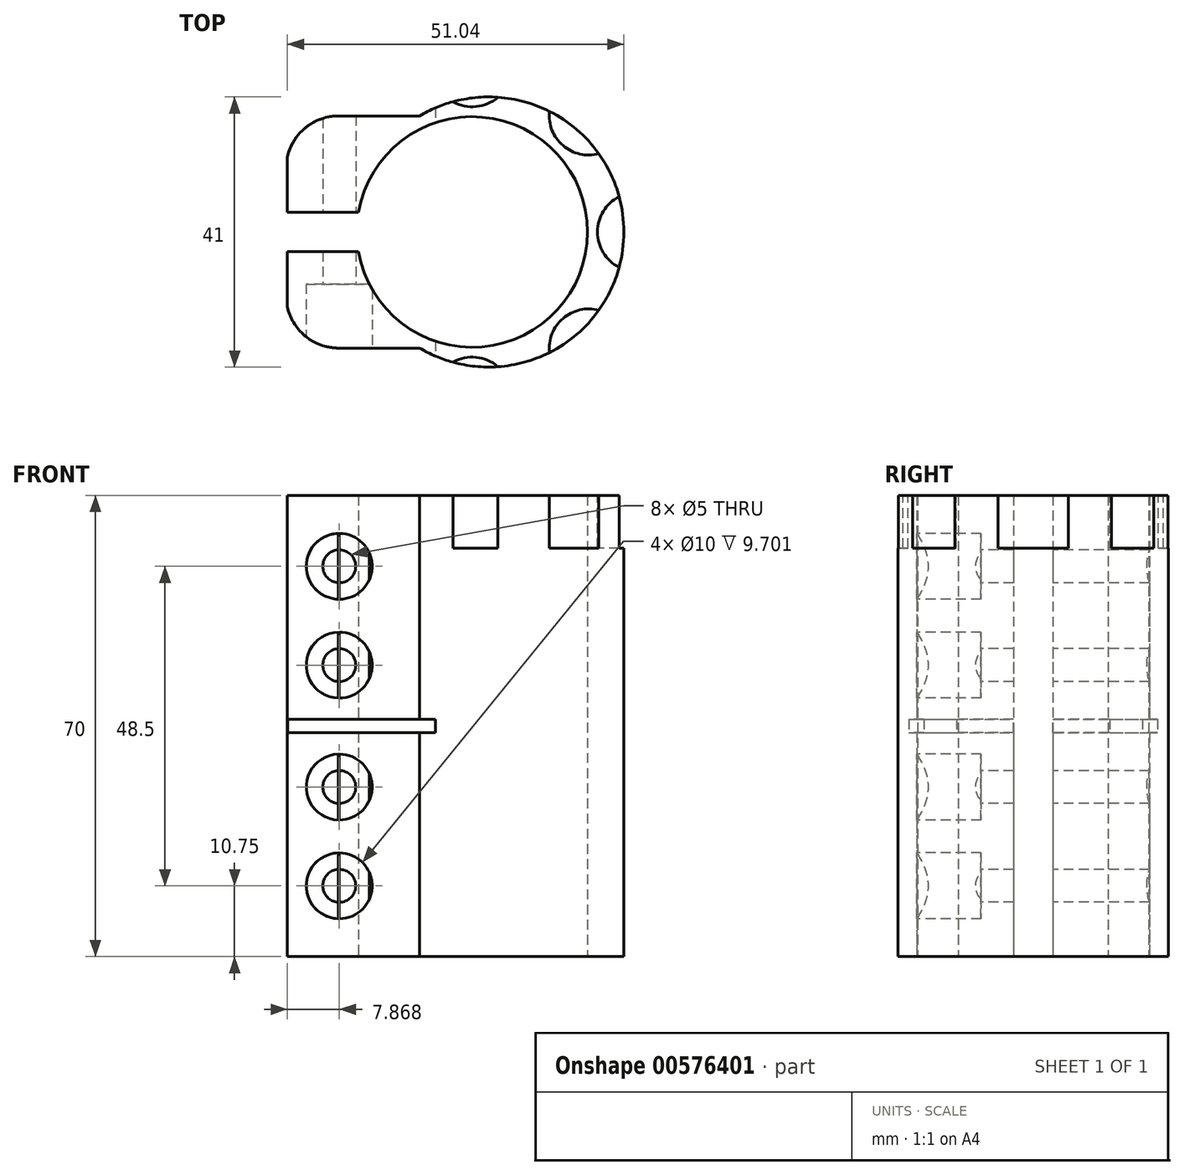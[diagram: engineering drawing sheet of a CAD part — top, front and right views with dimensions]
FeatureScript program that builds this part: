
annotation { "Feature Type Name" : "Feature", "Feature Type Description" : "" }
export const myFeature = defineFeature(function(context is Context, id is Id, definition is map)
    precondition{}
    {
        {
            var Q0;
            Q0=qCreatedBy(makeId("Top.planeOp"),FACE);
            var sketch = newSketch(context, id + "F0", { "sketchPlane" : qUnion([Q0])});
            skArc(sketch, "E0", {"start": v(-17.24, -2.98) * mm, "mid": v(17.5, 0) * mm, "end": v(-17.24, 2.98) * mm});
            skLineSegment(sketch, "E1", {"start": v(-7.97, 17.62) * mm, "end": v(-20.17, 17.62) * mm});
            skLineSegment(sketch, "E2", {"start": v(-28.04, 11.38) * mm, "end": v(-28.04, 2.98) * mm});
            skLineSegment(sketch, "E3", {"start": v(-28.04, 2.98) * mm, "end": v(-17.24, 2.98) * mm});
            skArc(sketch, "E4", {"start": v(-20.17, 17.62) * mm, "mid": v(-25.21, 15.9) * mm, "end": v(-28.04, 11.38) * mm});
            skLineSegment(sketch, "E5", {"start": v(0, 0) * mm, "end": v(37.47, 0) * mm});
            skLineSegment(sketch, "E6.MirrorCS", {"start": v(-28.04, -2.98) * mm, "end": v(-17.24, -2.98) * mm});
            skLineSegment(sketch, "E7.MirrorCS", {"start": v(-7.97, -17.62) * mm, "end": v(-20.17, -17.62) * mm});
            skLineSegment(sketch, "E8.MirrorCS", {"start": v(-28.04, -11.38) * mm, "end": v(-28.04, -2.98) * mm});
            skArc(sketch, "E9.MirrorCS", {"start": v(-20.17, -17.62) * mm, "mid": v(-25.21, -15.9) * mm, "end": v(-28.04, -11.38) * mm});
            skArc(sketch, "E10.trimOffspring", {"start": v(-7.97, -17.62) * mm, "mid": v(23, 0) * mm, "end": v(-7.97, 17.62) * mm});
            skSolve(sketch);
        }
        {
            var Q0;
            Q0 = qSketchRegion(id + "F0", true);
            extrude(context, id + "F1", {"entities" : qUnion([Q0]), "endBound" : BoundingType.SYMMETRIC, "depth" : 70 * mm, "offsetDistance" : 25 * mm});
        }
        {
            var Q0;
            Q0=makeQuery(id+"F1.opExtrude","SWEPT_FACE",FACE,{"disambiguationData":[OSD([sQuery(id+"F0.wireOp",EDGE,"E7.MirrorCS")])]});
            var sketch = newSketch(context, id + "F2", { "sketchPlane" : qUnion([Q0])});
            skPoint(sketch, "E11", {"position": v(-20.17, -9.25) * mm});
            skPoint(sketch, "E12", {"position": v(-20.17, -24.25) * mm});
            skPoint(sketch, "E13", {"position": v(-20.17, 9.25) * mm});
            skPoint(sketch, "E14", {"position": v(-20.17, 24.25) * mm});
            skSolve(sketch);
        }
        {
            var Q0;
            Q0=sQuery(id+"F2.wireOp",VERTEX,"E12");
            var Q1;
            Q1=sQuery(id+"F2.wireOp",VERTEX,"E11");
            var Q2;
            Q2=sQuery(id+"F2.wireOp",VERTEX,"E13");
            var Q3;
            Q3=sQuery(id+"F2.wireOp",VERTEX,"E14");
            var Q4;
            Q4=makeQuery(id+"F1.opExtrude","SWEPT_BODY",BODY,{"disambiguationData":[OSD([sQuery(id+"F0.wireOp",EDGE,"E0"),sQuery(id+"F0.wireOp",EDGE,"E1"),sQuery(id+"F0.wireOp",EDGE,"E2"),sQuery(id+"F0.wireOp",EDGE,"E3"),sQuery(id+"F0.wireOp",EDGE,"E4"),sQuery(id+"F0.wireOp",EDGE,"E6.MirrorCS"),sQuery(id+"F0.wireOp",EDGE,"E7.MirrorCS"),sQuery(id+"F0.wireOp",EDGE,"E8.MirrorCS"),sQuery(id+"F0.wireOp",EDGE,"E9.MirrorCS"),sQuery(id+"F0.wireOp",EDGE,"E10.trimOffspring")])]});
            hole(context, id + "F3", {"style" : HoleStyle.C_BORE, "endStyle" : HoleEndStyle.THROUGH, "holeDiameter" : 5 * mm, "cBoreDiameter" : 10 * mm, "cBoreDepth" : 8 * mm, "majorDiameter" : 5 * mm, "isTappedThrough" : true, "tappedDepth" : 12 * mm, "tapClearance" : 3, "locations" : qUnion([Q0, Q1, Q2, Q3]), "scope" : qUnion([Q4])});
        }
        {
            var Q0;
            Q0=qCreatedBy(makeId("Front.planeOp"),FACE);
            var sketch = newSketch(context, id + "F4", { "sketchPlane" : qUnion([Q0])});
            skLineSegment(sketch, "E15.bottom", {"start": v(-27.99, 1) * mm, "end": v(-5.59, 1) * mm});
            skLineSegment(sketch, "E15.top", {"start": v(-27.99, -1) * mm, "end": v(-5.59, -1) * mm});
            skLineSegment(sketch, "E15.left", {"start": v(-27.99, 1) * mm, "end": v(-27.99, -1) * mm});
            skLineSegment(sketch, "E15.right", {"start": v(-5.59, 1) * mm, "end": v(-5.59, -1) * mm});
            skSolve(sketch);
        }
        {
            var Q0;
            Q0 = qSketchRegion(id + "F4", true);
            extrude(context, id + "F5", {"entities" : qUnion([Q0]), "operationType" : NewBodyOperationType.REMOVE, "endBound" : BoundingType.SYMMETRIC, "oppositeDirection" : true, "depth" : 50 * mm, "offsetDistance" : 25 * mm});
        }
        {
            var Q0;
            Q0=makeQuery(id+"F1.opExtrude","CAP_FACE",FACE,{"disambiguationData":[OSD([sQuery(id+"F0.wireOp",EDGE,"E0"),sQuery(id+"F0.wireOp",EDGE,"E1"),sQuery(id+"F0.wireOp",EDGE,"E2"),sQuery(id+"F0.wireOp",EDGE,"E3"),sQuery(id+"F0.wireOp",EDGE,"E4"),sQuery(id+"F0.wireOp",EDGE,"E6.MirrorCS"),sQuery(id+"F0.wireOp",EDGE,"E7.MirrorCS"),sQuery(id+"F0.wireOp",EDGE,"E8.MirrorCS"),sQuery(id+"F0.wireOp",EDGE,"E9.MirrorCS"),sQuery(id+"F0.wireOp",EDGE,"E10.trimOffspring")])],"isStart":false});
            var sketch = newSketch(context, id + "F6", { "sketchPlane" : qUnion([Q0])});
            skCircle(sketch, "E16", {"center": v(0, -25) * mm, "radius": 6 * mm});
            skCircle(sketch, "E17.1.0", {"center": v(17.68, -17.68) * mm, "radius": 6 * mm});
            skCircle(sketch, "E17.2.0", {"center": v(25, 0) * mm, "radius": 6 * mm});
            skCircle(sketch, "E17.3.0", {"center": v(17.68, 17.68) * mm, "radius": 6 * mm});
            skCircle(sketch, "E17.4.0", {"center": v(0, 25) * mm, "radius": 6 * mm});
            skPoint(sketch, "E17.center", {"position": v(0, 0) * mm});
            skLineSegment(sketch, "E17.anchor1", {"start": v(0, 0) * mm, "end": v(0, -25) * mm, "construction": true});
            skLineSegment(sketch, "E17.anchor2", {"start": v(0, 0) * mm, "end": v(0, 25) * mm, "construction": true});
            skSolve(sketch);
        }
        {
            var Q0;
            Q0 = qSketchRegion(id + "F6", true);
            extrude(context, id + "F7", {"entities" : qUnion([Q0]), "operationType" : NewBodyOperationType.REMOVE, "oppositeDirection" : true, "depth" : 8 * mm, "offsetDistance" : 25 * mm});
        }
    });
